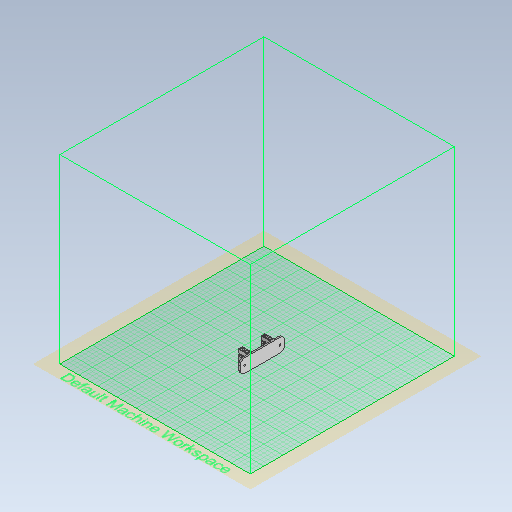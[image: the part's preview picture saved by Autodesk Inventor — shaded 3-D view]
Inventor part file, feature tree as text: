
AUTODESK INVENTOR PART (.ipt)
format: ipt  version: 2020 (Build 240168000, 168)  size: 472,064 bytes
history: native  units: mm
features: other x4, extrude x3, sketch x3, fillet x1, mirror x1, projected_geometry x1
ambient origin geometry x8: Origin, YZ Plane, XZ Plane, XY Plane, X Axis, Y Axis, Z Axis, Center Point
bodies: Solide1 (feature_tree)
feature tree (13):
  other  "servo_holder.ipt"
  extrude  "Extrusion1"  Depth=10.0mm
  extrude  "Extrusion2"  Depth=0.5mm TaperAngle=0.0deg
  fillet  "Congé1"  Radius=10.0mm
  extrude  "Extrusion3"  Depth=10.0mm
  other  "Plan de construction2"
  mirror  "Symétrie1"
  other  "Solide1::servo_holder.ipt"
  other  "FonctionRepérage1"
  sketch  "Esquisse1"
  projected_geometry  "Boucle projetée1"
  sketch  "Esquisse2"
  sketch  "Esquisse3"
